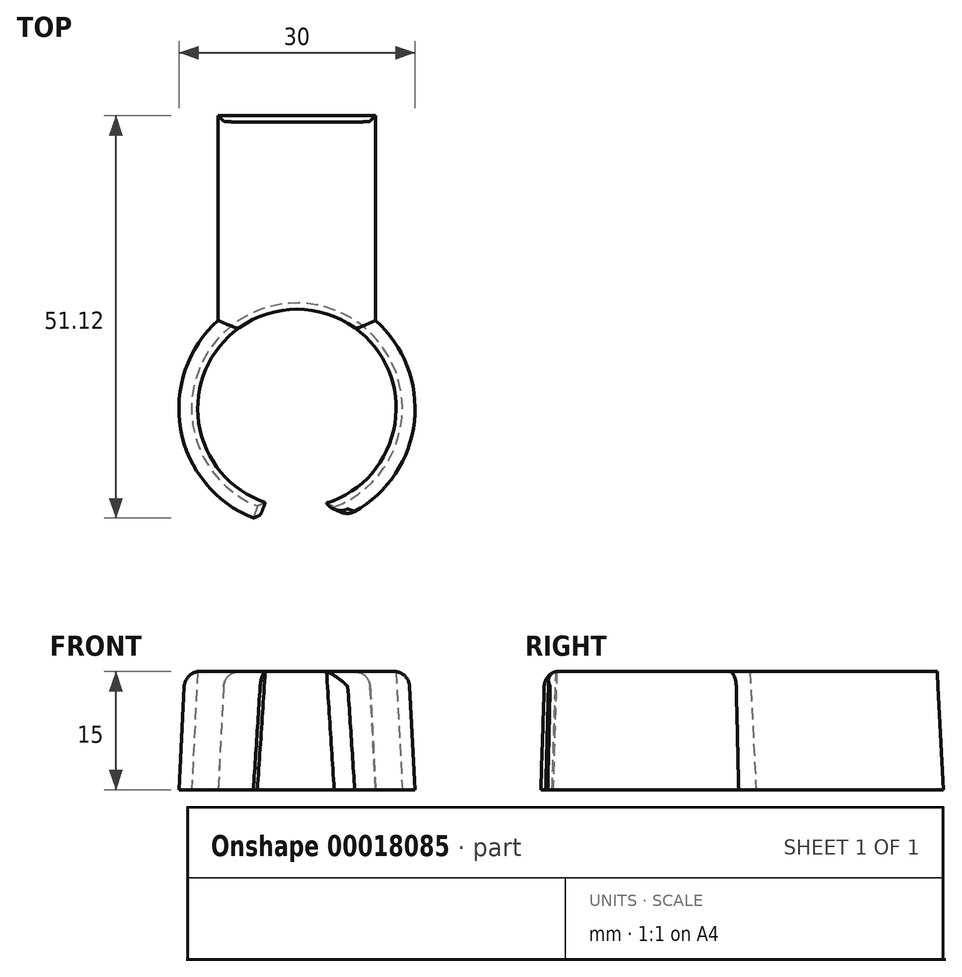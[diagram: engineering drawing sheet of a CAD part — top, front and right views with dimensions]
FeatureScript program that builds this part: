
annotation { "Feature Type Name" : "Feature", "Feature Type Description" : "" }
export const myFeature = defineFeature(function(context is Context, id is Id, definition is map)
    precondition{}
    {
        {
            var Q0;
            Q0=qCreatedBy(makeId("Top.planeOp"),FACE);
            var sketch = newSketch(context, id + "F3", { "sketchPlane" : qUnion([Q0])});
            skCircle(sketch, "E0", {"center": v(0, 0) * mm, "radius": 12.5 * mm, "construction": true});
            skArc(sketch, "E1", {"start": v(-10, 11.18) * mm, "mid": v(0, -15) * mm, "end": v(10, 11.18) * mm});
            skLineSegment(sketch, "E2.top", {"start": v(-10, 37.18) * mm, "end": v(10, 37.18) * mm});
            skLineSegment(sketch, "E2.left", {"start": v(-10, 11.18) * mm, "end": v(-10, 37.18) * mm});
            skLineSegment(sketch, "E2.right", {"start": v(10, 11.18) * mm, "end": v(10, 37.18) * mm});
            skSolve(sketch);
        }
        {
            var Q0;
            Q0 = qSketchRegion(id + "F3", true);
            extrude(context, id + "F4", {"entities" : qUnion([Q0]), "depth" : 15 * mm, "hasDraft" : true, "draftAngle" : 3 * degree, "draftPullDirection" : true});
        }
        {
            var Q0;
            Q0=makeQuery(id+"F4.opExtrude","CAP_FACE",FACE,{"disambiguationData":[OSD([sQuery(id+"F3.wireOp",EDGE,"E1"),sQuery(id+"F3.wireOp",EDGE,"E2.top"),sQuery(id+"F3.wireOp",EDGE,"E2.left"),sQuery(id+"F3.wireOp",EDGE,"E2.right")])],"isStart":false});
            var sketch = newSketch(context, id + "F5", { "sketchPlane" : qUnion([Q0])});
            skCircle(sketch, "E3", {"center": v(0, 0) * mm, "radius": 12.6 * mm});
            skSolve(sketch);
        }
        {
            var Q0;
            Q0 = qSketchRegion(id + "F5", true);
            extrude(context, id + "F0", {"entities" : qUnion([Q0]), "operationType" : NewBodyOperationType.REMOVE, "oppositeDirection" : true, "depth" : 25 * mm, "hasDraft" : true, "draftAngle" : 3 * degree});
        }
        {
            var Q0;
            Q0=makeQuery(id+"F4.opExtrude","CAP_FACE",FACE,{"disambiguationData":[OSD([sQuery(id+"F3.wireOp",EDGE,"E1"),sQuery(id+"F3.wireOp",EDGE,"E2.top"),sQuery(id+"F3.wireOp",EDGE,"E2.left"),sQuery(id+"F3.wireOp",EDGE,"E2.right")])],"isStart":false});
            var sketch = newSketch(context, id + "F6", { "sketchPlane" : qUnion([Q0])});
            skLineSegment(sketch, "E4", {"start": v(0, 0) * mm, "end": v(-6.07, -18) * mm});
            skLineSegment(sketch, "E5", {"start": v(-6.07, -18) * mm, "end": v(0, 0) * mm});
            skLineSegment(sketch, "E6", {"start": v(5.63, -18) * mm, "end": v(0, 0) * mm});
            skLineSegment(sketch, "E7", {"start": v(-6.07, -18) * mm, "end": v(5.63, -18) * mm});
            skSolve(sketch);
        }
        {
            var Q0;
            Q0 = qSketchRegion(id + "F6", true);
            extrude(context, id + "F1", {"entities" : qUnion([Q0]), "operationType" : NewBodyOperationType.REMOVE, "oppositeDirection" : true, "depth" : 25 * mm, "hasDraft" : true, "draftAngle" : 3 * degree});
        }
        {
            var Q0;
            {var subQ0=sQuery(id+"F3.wireOp",EDGE,"E1");var subQ1=sQuery(id+"F3.wireOp",EDGE,"E2.left");Q0=makeQuery(id+"F1.boolean.opBoolean","SPLIT",EDGE,{"disambiguationData":[TD([makeQuery(id+"F4.opExtrude","SWEPT_FACE",FACE,{"disambiguationData":[OSD([subQ1])]})])],"derivedFrom":makeQuery(id+"F4.opExtrude","CAP_EDGE",EDGE,{"disambiguationData":[OSD([subQ0])],"isStart":false})});}
            var Q1;
            Q1=makeQuery(id+"F1.boolean.opBoolean","INTERSECT",EDGE,{"derivedFrom":[makeQuery(id+"F4.opExtrude","SWEPT_FACE",FACE,{"disambiguationData":[OSD([sQuery(id+"F3.wireOp",EDGE,"E1")])]}),makeQuery(id+"F1.opExtrude","SWEPT_FACE",FACE,{"disambiguationData":[OSD([sQuery(id+"F6.wireOp",EDGE,"E5")])]})]});
            var Q2;
            Q2=makeQuery(id+"F1.boolean.opBoolean","INTERSECT",EDGE,{"derivedFrom":[makeQuery(id+"F4.opExtrude","SWEPT_FACE",FACE,{"disambiguationData":[OSD([sQuery(id+"F3.wireOp",EDGE,"E1")])]}),makeQuery(id+"F1.opExtrude","SWEPT_FACE",FACE,{"disambiguationData":[OSD([sQuery(id+"F6.wireOp",EDGE,"E6")])]})]});
            var Q3;
            {var subQ0=sQuery(id+"F3.wireOp",EDGE,"E1");var subQ1=sQuery(id+"F3.wireOp",EDGE,"E2.right");Q3=makeQuery(id+"F1.boolean.opBoolean","SPLIT",EDGE,{"disambiguationData":[TD([makeQuery(id+"F4.opExtrude","SWEPT_FACE",FACE,{"disambiguationData":[OSD([subQ1])]})])],"derivedFrom":makeQuery(id+"F4.opExtrude","CAP_EDGE",EDGE,{"disambiguationData":[OSD([subQ0])],"isStart":false})});}
            var Q4;
            Q4=makeQuery(id+"F4.opExtrude","CAP_EDGE",EDGE,{"disambiguationData":[OSD([sQuery(id+"F3.wireOp",EDGE,"E2.right")])],"isStart":false});
            var Q5;
            Q5=makeQuery(id+"F4.opExtrude","CAP_EDGE",EDGE,{"disambiguationData":[OSD([sQuery(id+"F3.wireOp",EDGE,"E2.left")])],"isStart":false});
            fillet(context, id + "F2", {"entities" : qUnion([Q0, Q1, Q2, Q3, Q4, Q5]), "radius" : 2 * mm, "tangentPropagation" : true, "allowEdgeOverflow" : false});
        }
    });
